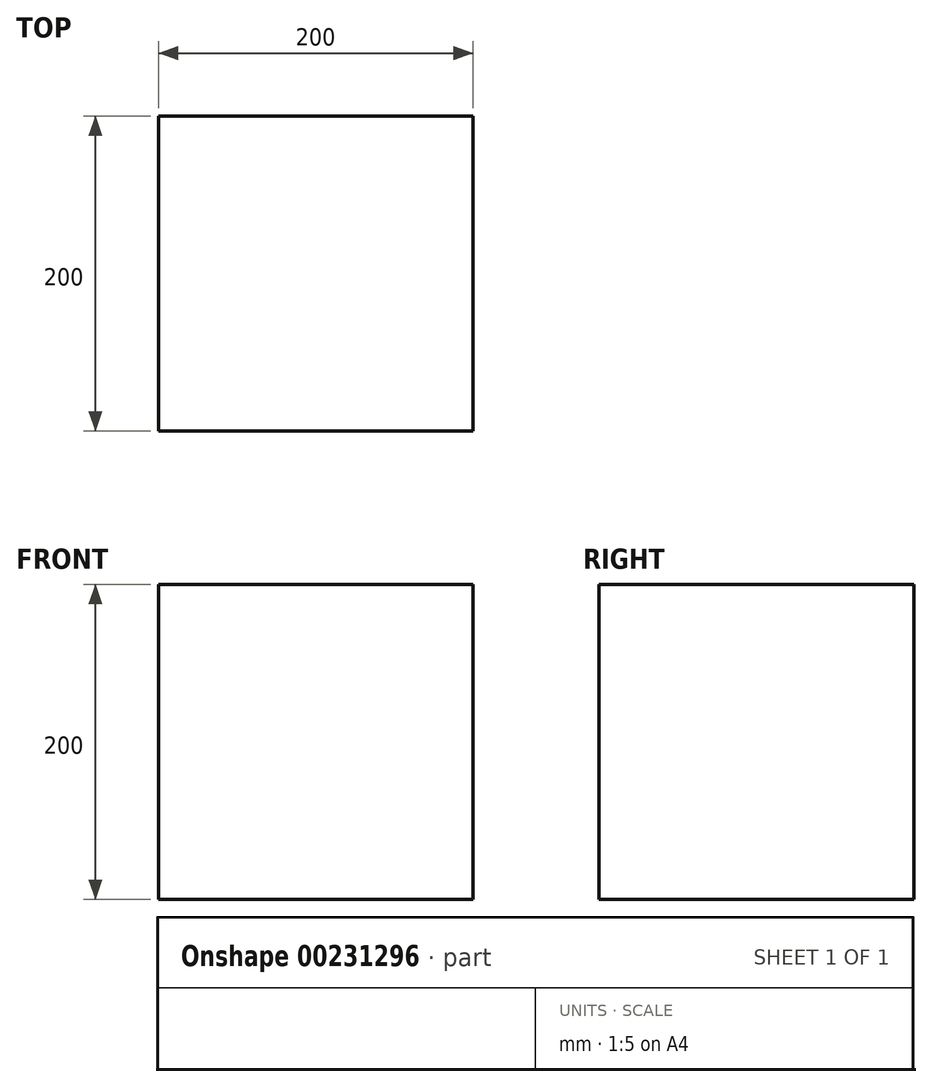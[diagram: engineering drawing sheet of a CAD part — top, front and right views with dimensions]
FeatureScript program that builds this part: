
annotation { "Feature Type Name" : "Feature", "Feature Type Description" : "" }
export const myFeature = defineFeature(function(context is Context, id is Id, definition is map)
    precondition{}
    {
        {
            var Q0;
            Q0=qCreatedBy(makeId("Top.planeOp"),FACE);
            var sketch = newSketch(context, id + "F0", { "sketchPlane" : qUnion([Q0])});
            skLineSegment(sketch, "E0.bottom", {"start": v(-98.2, -95.4) * mm, "end": v(101.8, -95.4) * mm});
            skLineSegment(sketch, "E0.top", {"start": v(-98.2, 104.6) * mm, "end": v(101.8, 104.6) * mm});
            skLineSegment(sketch, "E0.left", {"start": v(-98.2, -95.4) * mm, "end": v(-98.2, 104.6) * mm});
            skLineSegment(sketch, "E0.right", {"start": v(101.8, -95.4) * mm, "end": v(101.8, 104.6) * mm});
            skSolve(sketch);
        }
        {
            var Q0;
            Q0=makeQuery(id+"F0.imprint","IMPRINT",FACE,{"disambiguationData":[TD([[makeQuery(id+"F0.imprint","IMPRINT",EDGE,{"derivedFrom":sQuery(id+"F0.wireOp",EDGE,"E0.bottom")}),1.0]])]});
            extrude(context, id + "F1", {"entities" : qUnion([Q0]), "depth" : 200 * mm});
        }
    });
